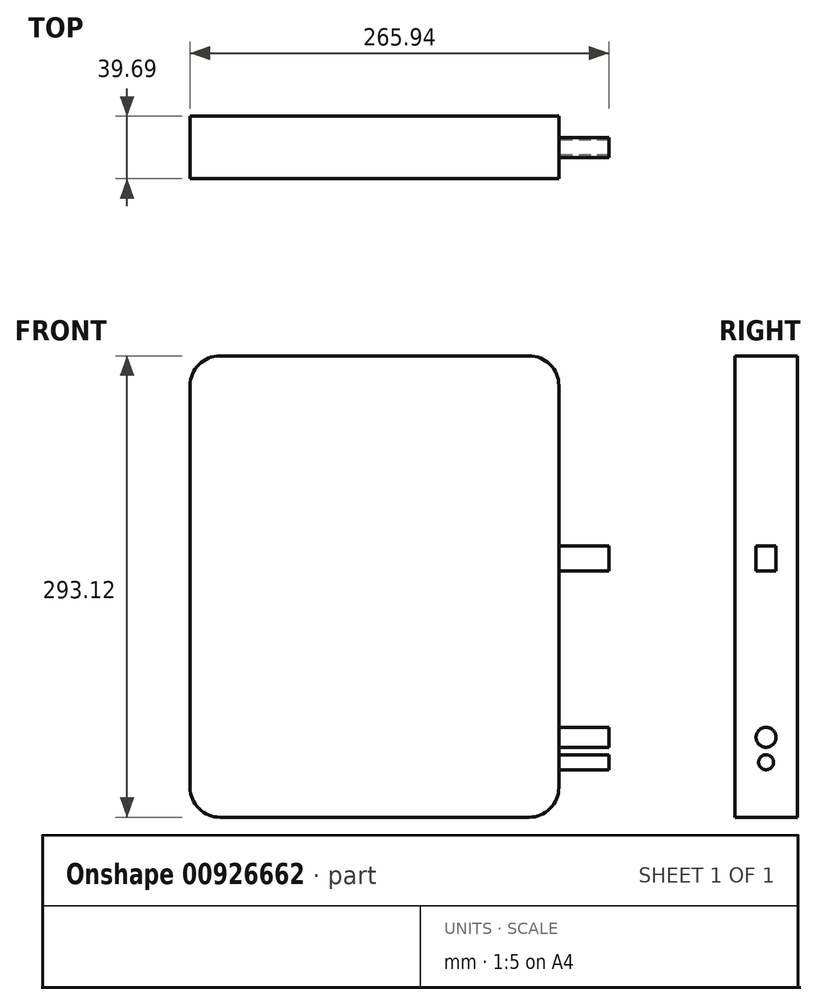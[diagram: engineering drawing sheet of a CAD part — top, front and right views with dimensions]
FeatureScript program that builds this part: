
annotation { "Feature Type Name" : "Feature", "Feature Type Description" : "" }
export const myFeature = defineFeature(function(context is Context, id is Id, definition is map)
    precondition{}
    {
        {
            var Q0;
            Q0=qCreatedBy(makeId("Front.planeOp"),FACE);
            var sketch = newSketch(context, id + "F0", { "sketchPlane" : qUnion([Q0])});
            skLineSegment(sketch, "E0.bottom", {"start": v(-116.57, 137.62) * mm, "end": v(117.62, 137.62) * mm});
            skLineSegment(sketch, "E0.top", {"start": v(-116.57, -155.5) * mm, "end": v(117.62, -155.5) * mm});
            skLineSegment(sketch, "E0.left", {"start": v(-116.57, 137.62) * mm, "end": v(-116.57, -155.5) * mm});
            skLineSegment(sketch, "E0.right", {"start": v(117.62, 137.62) * mm, "end": v(117.62, -155.5) * mm});
            skSolve(sketch);
        }
        {
            var Q0;
            Q0 = qSketchRegion(id + "F0", true);
            extrude(context, id + "F1", {"entities" : qUnion([Q0]), "depth" : 39.69 * mm, "offsetDistance" : 25.4 * mm});
        }
        {
            var Q0;
            Q0=makeQuery(id+"F1.opExtrude","SWEPT_EDGE",EDGE,{"disambiguationData":[OSD([sQuery(id+"F0.wireOp",EDGE,"E0.bottom"),sQuery(id+"F0.wireOp",EDGE,"E0.right")])]});
            fillet(context, id + "F2", {"entities" : qUnion([Q0]), "radius" : 19.05 * mm, "tangentPropagation" : true, "allowEdgeOverflow" : false});
        }
        {
            var Q0;
            Q0=makeQuery(id+"F1.opExtrude","SWEPT_EDGE",EDGE,{"disambiguationData":[OSD([sQuery(id+"F0.wireOp",EDGE,"E0.bottom"),sQuery(id+"F0.wireOp",EDGE,"E0.left")])]});
            fillet(context, id + "F3", {"entities" : qUnion([Q0]), "radius" : 19.05 * mm, "tangentPropagation" : true, "allowEdgeOverflow" : false});
        }
        {
            var Q0;
            Q0=makeQuery(id+"F1.opExtrude","SWEPT_EDGE",EDGE,{"disambiguationData":[OSD([sQuery(id+"F0.wireOp",EDGE,"E0.top"),sQuery(id+"F0.wireOp",EDGE,"E0.left")])]});
            fillet(context, id + "F4", {"entities" : qUnion([Q0]), "radius" : 19.05 * mm, "tangentPropagation" : true, "allowEdgeOverflow" : false});
        }
        {
            var Q0;
            Q0=makeQuery(id+"F1.opExtrude","SWEPT_EDGE",EDGE,{"disambiguationData":[OSD([sQuery(id+"F0.wireOp",EDGE,"E0.top"),sQuery(id+"F0.wireOp",EDGE,"E0.right")])]});
            fillet(context, id + "F5", {"entities" : qUnion([Q0]), "radius" : 19.05 * mm, "tangentPropagation" : true, "allowEdgeOverflow" : false});
        }
        {
            var Q0;
            Q0=makeQuery(id+"F1.opExtrude","SWEPT_FACE",FACE,{"disambiguationData":[OSD([sQuery(id+"F0.wireOp",EDGE,"E0.right")])]});
            var sketch = newSketch(context, id + "F6", { "sketchPlane" : qUnion([Q0])});
            skCircle(sketch, "E1", {"center": v(-19.84, -104.7) * mm, "radius": 6.35 * mm});
            skSolve(sketch);
        }
        {
            var Q0;
            Q0=makeQuery(id+"F6.imprint","IMPRINT",FACE,{"disambiguationData":[TD([[makeQuery(id+"F6.imprint","IMPRINT",EDGE,{"derivedFrom":sQuery(id+"F6.wireOp",EDGE,"E1")}),1.0]])]});
            extrude(context, id + "F7", {"entities" : qUnion([Q0]), "operationType" : NewBodyOperationType.ADD, "depth" : 31.75 * mm, "offsetDistance" : 25.4 * mm});
        }
        {
            var Q0;
            Q0=makeQuery(id+"F1.opExtrude","SWEPT_FACE",FACE,{"disambiguationData":[OSD([sQuery(id+"F0.wireOp",EDGE,"E0.right")])]});
            var sketch = newSketch(context, id + "F8", { "sketchPlane" : qUnion([Q0])});
            skCircle(sketch, "E2", {"center": v(-19.84, -120.57) * mm, "radius": 4.76 * mm});
            skSolve(sketch);
        }
        {
            var Q0;
            Q0 = qSketchRegion(id + "F8", true);
            extrude(context, id + "F9", {"entities" : qUnion([Q0]), "operationType" : NewBodyOperationType.ADD, "depth" : 31.75 * mm, "offsetDistance" : 25.4 * mm});
        }
        {
            var Q0;
            Q0=makeQuery(id+"F1.opExtrude","SWEPT_FACE",FACE,{"disambiguationData":[OSD([sQuery(id+"F0.wireOp",EDGE,"E0.right")])]});
            var sketch = newSketch(context, id + "F10", { "sketchPlane" : qUnion([Q0])});
            skLineSegment(sketch, "E3.bottom", {"start": v(-26.2, 16.97) * mm, "end": v(-13.5, 16.97) * mm});
            skLineSegment(sketch, "E3.top", {"start": v(-26.2, 1.1) * mm, "end": v(-13.5, 1.1) * mm});
            skLineSegment(sketch, "E3.left", {"start": v(-26.2, 16.97) * mm, "end": v(-26.2, 1.1) * mm});
            skLineSegment(sketch, "E3.right", {"start": v(-13.5, 16.97) * mm, "end": v(-13.5, 1.1) * mm});
            skSolve(sketch);
        }
        {
            var Q0;
            Q0=makeQuery(id+"F10.imprint","IMPRINT",FACE,{"disambiguationData":[TD([[makeQuery(id+"F10.imprint","IMPRINT",EDGE,{"derivedFrom":sQuery(id+"F10.wireOp",EDGE,"E3.bottom")}),-1.0]])]});
            extrude(context, id + "F11", {"entities" : qUnion([Q0]), "operationType" : NewBodyOperationType.ADD, "depth" : 31.75 * mm, "offsetDistance" : 25.4 * mm});
        }
    });
